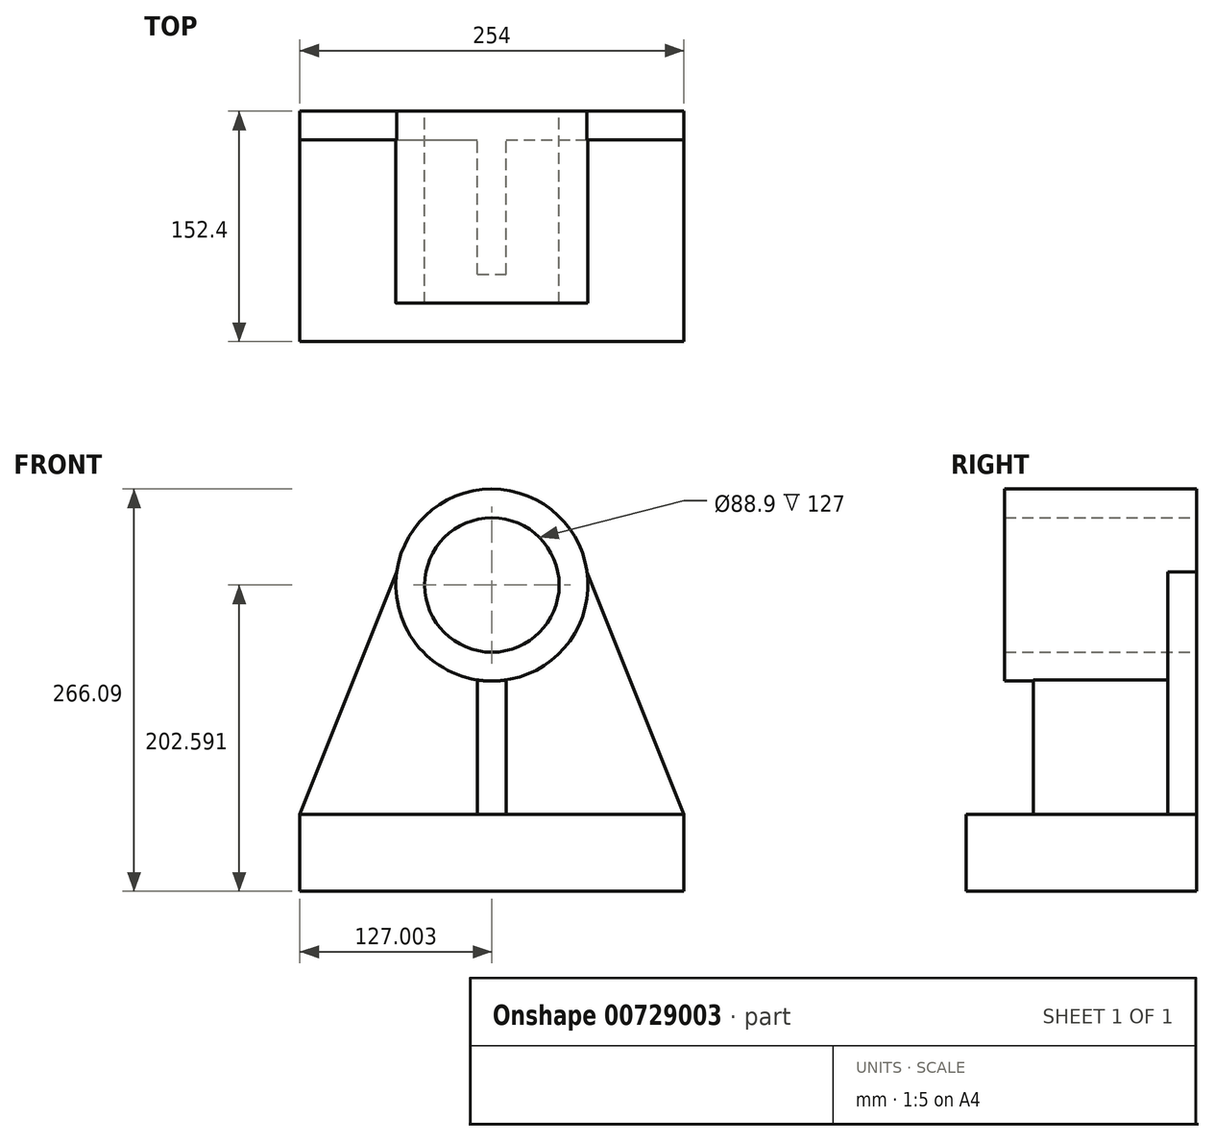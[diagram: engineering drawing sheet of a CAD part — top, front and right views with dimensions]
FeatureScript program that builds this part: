
annotation { "Feature Type Name" : "Feature", "Feature Type Description" : "" }
export const myFeature = defineFeature(function(context is Context, id is Id, definition is map)
    precondition{}
    {
        {
            var Q0;
            Q0=qCreatedBy(makeId("Front.planeOp"),FACE);
            var sketch = newSketch(context, id + "F0", { "sketchPlane" : qUnion([Q0])});
            skCircle(sketch, "E0", {"center": v(-47.66, -40.9) * mm, "radius": 63.5 * mm});
            skCircle(sketch, "E1", {"center": v(-47.66, -40.9) * mm, "radius": 44.45 * mm});
            skLineSegment(sketch, "E2", {"start": v(-57.18, -103.7) * mm, "end": v(-57.18, -192.7) * mm});
            skLineSegment(sketch, "E3", {"start": v(-38.13, -103.7) * mm, "end": v(-38.13, -192.7) * mm});
            skLineSegment(sketch, "E4", {"start": v(-174.66, -243.5) * mm, "end": v(-174.66, -192.7) * mm});
            skLineSegment(sketch, "E5", {"start": v(-174.66, -192.7) * mm, "end": v(79.34, -192.7) * mm});
            skLineSegment(sketch, "E6", {"start": v(79.34, -192.7) * mm, "end": v(79.34, -243.5) * mm});
            skPoint(sketch, "E7.orphan", {"position": v(-47.66, -243.5) * mm});
            skPoint(sketch, "E8.orphan", {"position": v(-57.18, -40.9) * mm});
            skPoint(sketch, "E9.orphan", {"position": v(-38.13, -40.9) * mm});
            skLineSegment(sketch, "E10", {"start": v(-174.66, -243.5) * mm, "end": v(79.34, -243.5) * mm});
            skLineSegment(sketch, "E11", {"start": v(-174.66, -192.7) * mm, "end": v(-110.54, -32.08) * mm});
            skLineSegment(sketch, "E12", {"start": v(15.23, -32.08) * mm, "end": v(79.34, -192.7) * mm});
            skSolve(sketch);
        }
        {
            var Q0;
            {var subQ4=sQuery(id+"F0.wireOp",EDGE,"E4");Q0=makeQuery(id+"F0.imprint","IMPRINT",FACE,{"disambiguationData":[TD([[makeQuery(id+"F0.imprint","IMPRINT",EDGE,{"derivedFrom":subQ4}),-1.0]])]});}
            extrude(context, id + "F1", {"entities" : qUnion([Q0]), "depth" : 152.4 * mm, "offsetDistance" : 25.4 * mm});
        }
        {
            var Q0;
            {var subQ0=sQuery(id+"F0.wireOp",EDGE,"E2");Q0=makeQuery(id+"F0.imprint","IMPRINT",FACE,{"disambiguationData":[TD([[makeQuery(id+"F0.imprint","IMPRINT",EDGE,{"derivedFrom":subQ0}),-1.0]])]});}
            var Q1;
            {var subQ0=sQuery(id+"F0.wireOp",EDGE,"E3");Q1=makeQuery(id+"F0.imprint","IMPRINT",FACE,{"disambiguationData":[TD([[makeQuery(id+"F0.imprint","IMPRINT",EDGE,{"derivedFrom":subQ0}),1.0]])]});}
            extrude(context, id + "F2", {"entities" : qUnion([Q0, Q1]), "operationType" : NewBodyOperationType.ADD, "depth" : 19.05 * mm, "offsetDistance" : 25.4 * mm});
        }
        {
            var Q0;
            Q0=makeQuery(id+"F0.imprint","IMPRINT",FACE,{"disambiguationData":[TD([[makeQuery(id+"F0.imprint","IMPRINT",EDGE,{"derivedFrom":sQuery(id+"F0.wireOp",EDGE,"E1")}),-1.0]])]});
            extrude(context, id + "F3", {"entities" : qUnion([Q0]), "operationType" : NewBodyOperationType.ADD, "depth" : 127 * mm, "offsetDistance" : 25.4 * mm});
        }
        {
            var Q0;
            {var subQ0=sQuery(id+"F0.wireOp",EDGE,"E2");Q0=makeQuery(id+"F0.imprint","IMPRINT",FACE,{"disambiguationData":[TD([[makeQuery(id+"F0.imprint","IMPRINT",EDGE,{"derivedFrom":subQ0}),1.0]])]});}
            extrude(context, id + "F4", {"entities" : qUnion([Q0]), "operationType" : NewBodyOperationType.ADD, "depth" : 107.95 * mm, "offsetDistance" : 25.4 * mm});
        }
    });
